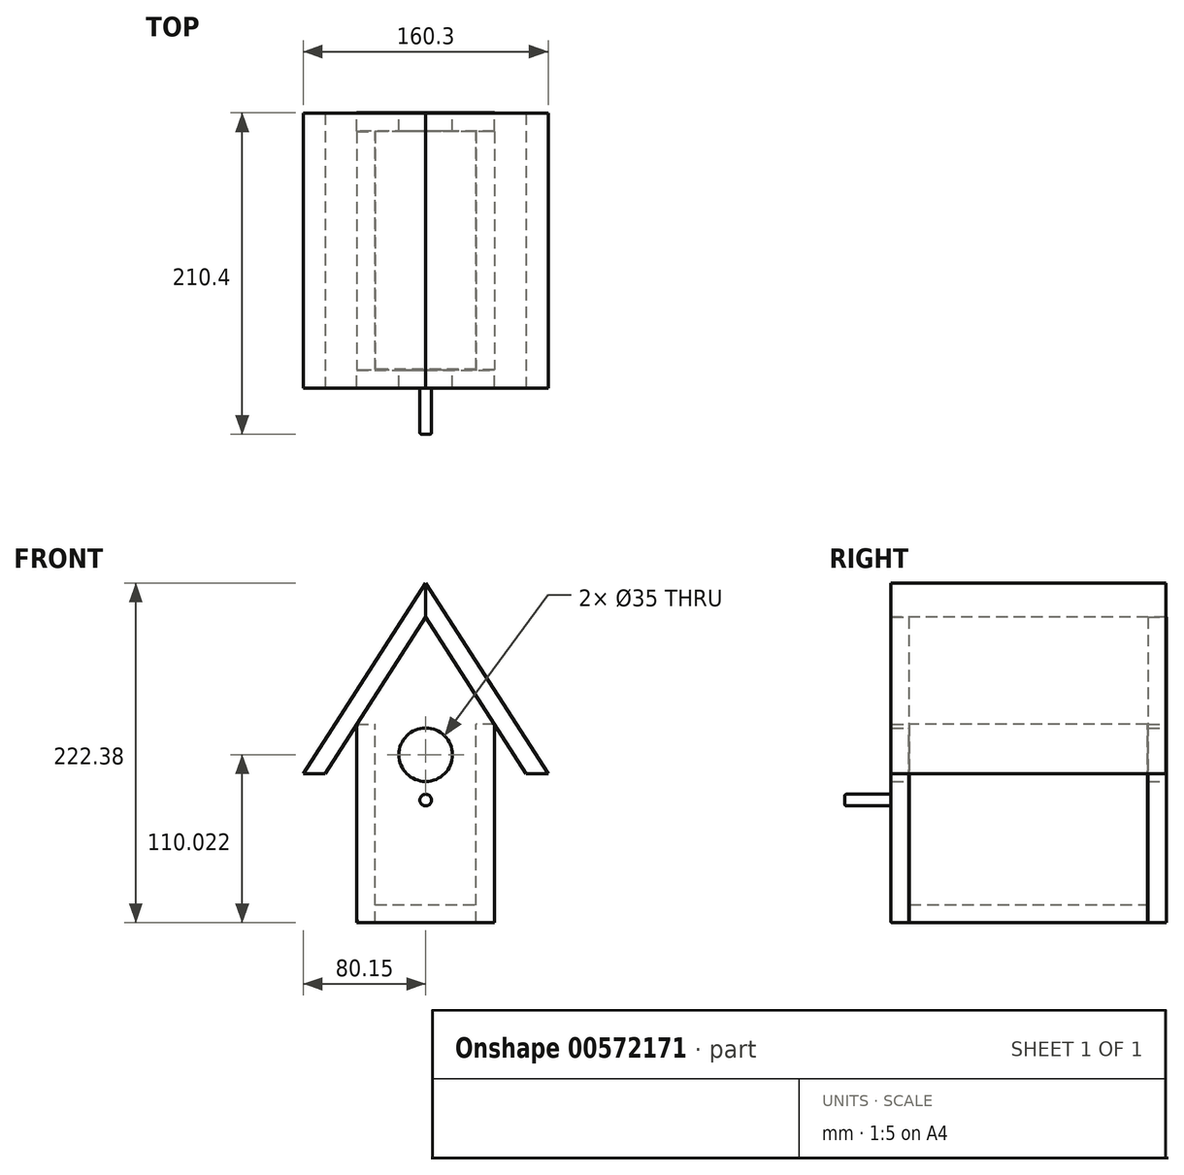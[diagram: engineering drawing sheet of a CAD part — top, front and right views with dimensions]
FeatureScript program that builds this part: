
annotation { "Feature Type Name" : "Feature", "Feature Type Description" : "" }
export const myFeature = defineFeature(function(context is Context, id is Id, definition is map)
    precondition{}
    {
        {
            var Q0;
            Q0=qCreatedBy(makeId("Front.planeOp"),FACE);
            var sketch = newSketch(context, id + "F0", { "sketchPlane" : qUnion([Q0])});
            skLineSegment(sketch, "E0.top", {"start": v(45, -65) * mm, "end": v(-45, -65) * mm});
            skLineSegment(sketch, "E0.left", {"start": v(45, 65) * mm, "end": v(45, -65) * mm});
            skLineSegment(sketch, "E0.right", {"start": v(-45, 65) * mm, "end": v(-45, -65) * mm});
            skPoint(sketch, "E0.middle", {"position": v(0, 0) * mm});
            skLineSegment(sketch, "E1", {"start": v(-45, 65) * mm, "end": v(0, 135) * mm});
            skLineSegment(sketch, "E2", {"start": v(0, 135) * mm, "end": v(45, 65) * mm});
            skLineSegment(sketch, "E3", {"start": v(0, 135) * mm, "end": v(0, -65) * mm, "construction": true});
            skCircle(sketch, "E4", {"center": v(0, 45.02) * mm, "radius": 17.5 * mm});
            skLineSegment(sketch, "E5", {"start": v(0, 135) * mm, "end": v(0, 201.69) * mm, "construction": true});
            skLineSegment(sketch, "E6", {"start": v(0, 45.02) * mm, "end": v(-107.5, 45.02) * mm, "construction": true});
            skLineSegment(sketch, "E7", {"start": v(0, 45.02) * mm, "end": v(114.17, 45.02) * mm, "construction": true});
            skSolve(sketch);
        }
        {
            var Q0;
            Q0=makeQuery(id+"F0.imprint","IMPRINT",FACE,{"disambiguationData":[TD([[makeQuery(id+"F0.imprint","IMPRINT",EDGE,{"derivedFrom":sQuery(id+"F0.wireOp",EDGE,"E0.top")}),-1.0]])]});
            extrude(context, id + "F1", {"entities" : qUnion([Q0]), "depth" : 12 * mm, "offsetDistance" : 25 * mm});
        }
        {
            var Q0;
            Q0=makeQuery(id+"F1.opExtrude","CAP_FACE",FACE,{"disambiguationData":[OSD([sQuery(id+"F0.wireOp",EDGE,"E0.top"),sQuery(id+"F0.wireOp",EDGE,"E0.left"),sQuery(id+"F0.wireOp",EDGE,"E0.right"),sQuery(id+"F0.wireOp",EDGE,"E1"),sQuery(id+"F0.wireOp",EDGE,"E2"),sQuery(id+"F0.wireOp",EDGE,"E4")])],"isStart":false});
            var sketch = newSketch(context, id + "F2", { "sketchPlane" : qUnion([Q0])});
            skLineSegment(sketch, "E8", {"start": v(0, 157.38) * mm, "end": v(80.15, 32.7) * mm});
            skLineSegment(sketch, "E9", {"start": v(80.15, 32.7) * mm, "end": v(65.76, 32.7) * mm});
            skLineSegment(sketch, "E10", {"start": v(65.76, 32.7) * mm, "end": v(0, 135) * mm});
            skLineSegment(sketch, "E11", {"start": v(0, 157.38) * mm, "end": v(0, 135) * mm});
            skLineSegment(sketch, "E12.MirrorCS", {"start": v(-65.76, 32.7) * mm, "end": v(0, 135) * mm});
            skLineSegment(sketch, "E13.MirrorCS", {"start": v(0, 157.38) * mm, "end": v(-80.15, 32.7) * mm});
            skLineSegment(sketch, "E14.MirrorCS", {"start": v(-80.15, 32.7) * mm, "end": v(-65.76, 32.7) * mm});
            skSolve(sketch);
        }
        {
            var Q0;
            Q0=makeQuery(id+"F2.imprint","IMPRINT",FACE,{"disambiguationData":[TD([[makeQuery(id+"F2.imprint","IMPRINT",EDGE,{"derivedFrom":sQuery(id+"F2.wireOp",EDGE,"E11")}),-1.0]])]});
            extrude(context, id + "F3", {"entities" : qUnion([Q0]), "oppositeDirection" : true, "depth" : 180 * mm, "offsetDistance" : 25 * mm});
        }
        {
            var Q0;
            Q0=makeQuery(id+"F2.imprint","IMPRINT",FACE,{"disambiguationData":[TD([[makeQuery(id+"F2.imprint","IMPRINT",EDGE,{"derivedFrom":sQuery(id+"F2.wireOp",EDGE,"E8")}),-1.0]])]});
            extrude(context, id + "F4", {"entities" : qUnion([Q0]), "oppositeDirection" : true, "depth" : 180 * mm, "offsetDistance" : 25 * mm});
        }
        {
            var Q0;
            Q0=makeQuery(id+"F1.opExtrude","CAP_FACE",FACE,{"disambiguationData":[OSD([sQuery(id+"F0.wireOp",EDGE,"E0.top"),sQuery(id+"F0.wireOp",EDGE,"E0.left"),sQuery(id+"F0.wireOp",EDGE,"E0.right"),sQuery(id+"F0.wireOp",EDGE,"E1"),sQuery(id+"F0.wireOp",EDGE,"E2"),sQuery(id+"F0.wireOp",EDGE,"E4")])],"isStart":false});
            var sketch = newSketch(context, id + "F5", { "sketchPlane" : qUnion([Q0])});
            skLineSegment(sketch, "E15.bottom", {"start": v(45, -65) * mm, "end": v(33, -65) * mm});
            skLineSegment(sketch, "E15.top", {"start": v(45, 65) * mm, "end": v(33, 65) * mm});
            skLineSegment(sketch, "E15.left", {"start": v(45, -65) * mm, "end": v(45, 65) * mm});
            skLineSegment(sketch, "E15.right", {"start": v(33, -65) * mm, "end": v(33, 65) * mm});
            skLineSegment(sketch, "E16", {"start": v(0, 0) * mm, "end": v(0, -56.81) * mm, "construction": true});
            skSolve(sketch);
        }
        {
            var Q0;
            Q0 = qSketchRegion(id + "F5", true);
            extrude(context, id + "F6", {"entities" : qUnion([Q0]), "oppositeDirection" : true, "depth" : 168 * mm, "offsetDistance" : 25 * mm, "hasSecondDirection" : true, "secondDirectionOppositeDirection" : true, "secondDirectionDepth" : 12.3 * mm});
        }
        {
            var Q0;
            Q0=makeQuery(id+"F6.opExtrude","SWEPT_BODY",BODY,{"disambiguationData":[OSD([sQuery(id+"F5.wireOp",EDGE,"E15.bottom"),sQuery(id+"F5.wireOp",EDGE,"E15.top"),sQuery(id+"F5.wireOp",EDGE,"E15.left"),sQuery(id+"F5.wireOp",EDGE,"E15.right")])]});
            var Q1;
            Q1=qCreatedBy(makeId("Right.planeOp"),FACE);
            mirror(context, id + "F7", {"operationType" : NewBodyOperationType.ADD, "entities" : qUnion([Q0]), "mirrorPlane" : qUnion([Q1])});
        }
        {
            var Q0;
            Q0=makeQuery(id+"F1.opExtrude","SWEPT_BODY",BODY,{"disambiguationData":[OSD([sQuery(id+"F0.wireOp",EDGE,"E0.top"),sQuery(id+"F0.wireOp",EDGE,"E0.left"),sQuery(id+"F0.wireOp",EDGE,"E0.right"),sQuery(id+"F0.wireOp",EDGE,"E1"),sQuery(id+"F0.wireOp",EDGE,"E2"),sQuery(id+"F0.wireOp",EDGE,"E4")])]});
            transform(context, id + "F8", {"entities" : qUnion([Q0]), "transformType" : TransformType.TRANSLATION_3D, "dx" : 0 * mm, "dy" : 168.4 * mm, "dz" : 0 * mm, "makeCopy" : true});
        }
        {
            var Q0;
            Q0=makeQuery(id+"F8.opPattern","COPY",FACE,{"derivedFrom":makeQuery(id+"F1.opExtrude","CAP_FACE",FACE,{"disambiguationData":[OSD([sQuery(id+"F0.wireOp",EDGE,"E0.top"),sQuery(id+"F0.wireOp",EDGE,"E0.left"),sQuery(id+"F0.wireOp",EDGE,"E0.right"),sQuery(id+"F0.wireOp",EDGE,"E1"),sQuery(id+"F0.wireOp",EDGE,"E2"),sQuery(id+"F0.wireOp",EDGE,"E4")])],"isStart":true}),"instanceName":"1"});
            var sketch = newSketch(context, id + "F9", { "sketchPlane" : qUnion([Q0])});
            skLineSegment(sketch, "E17.bottom", {"start": v(33, -65) * mm, "end": v(-33, -65) * mm});
            skLineSegment(sketch, "E17.top", {"start": v(33, -53) * mm, "end": v(-33, -53) * mm});
            skLineSegment(sketch, "E17.left", {"start": v(33, -65) * mm, "end": v(33, -53) * mm});
            skLineSegment(sketch, "E17.right", {"start": v(-33, -65) * mm, "end": v(-33, -53) * mm});
            skLineSegment(sketch, "E18", {"start": v(33, -59) * mm, "end": v(0, -59) * mm});
            skLineSegment(sketch, "E19", {"start": v(0, -59) * mm, "end": v(-33, -59) * mm});
            skSolve(sketch);
        }
        {
            var Q0;
            Q0 = qSketchRegion(id + "F9", true);
            extrude(context, id + "F10", {"entities" : qUnion([Q0]), "oppositeDirection" : true, "depth" : 168 * mm, "offsetDistance" : 25 * mm, "hasSecondDirection" : true, "secondDirectionOppositeDirection" : true, "secondDirectionDepth" : 12.3 * mm});
        }
        {
            var Q0;
            Q0=makeQuery(id+"F1.opExtrude","CAP_FACE",FACE,{"disambiguationData":[OSD([sQuery(id+"F0.wireOp",EDGE,"E0.top"),sQuery(id+"F0.wireOp",EDGE,"E0.left"),sQuery(id+"F0.wireOp",EDGE,"E0.right"),sQuery(id+"F0.wireOp",EDGE,"E1"),sQuery(id+"F0.wireOp",EDGE,"E2"),sQuery(id+"F0.wireOp",EDGE,"E4")])],"isStart":false});
            var sketch = newSketch(context, id + "F11", { "sketchPlane" : qUnion([Q0])});
            skCircle(sketch, "E20", {"center": v(0, 15.33) * mm, "radius": 3.8 * mm});
            skSolve(sketch);
        }
        {
            var Q0;
            Q0=makeQuery(id+"F11.imprint","IMPRINT",FACE,{"disambiguationData":[TD([[makeQuery(id+"F11.imprint","IMPRINT",EDGE,{"derivedFrom":sQuery(id+"F11.wireOp",EDGE,"E20")}),1.0]])]});
            extrude(context, id + "F12", {"entities" : qUnion([Q0]), "depth" : 30 * mm, "offsetDistance" : 25 * mm});
        }
        {
            var Q0;
            Q0=makeQuery(id+"F12.opExtrude","CAP_EDGE",EDGE,{"disambiguationData":[OSD([sQuery(id+"F11.wireOp",EDGE,"E20")])],"isStart":false});
            fillet(context, id + "F13", {"entities" : qUnion([Q0]), "radius" : 1 * mm, "tangentPropagation" : true, "allowEdgeOverflow" : false});
        }
        {
            var Q0;
            Q0=makeQuery(id+"F1.opExtrude","CAP_FACE",FACE,{"disambiguationData":[OSD([sQuery(id+"F0.wireOp",EDGE,"E0.top"),sQuery(id+"F0.wireOp",EDGE,"E0.left"),sQuery(id+"F0.wireOp",EDGE,"E0.right"),sQuery(id+"F0.wireOp",EDGE,"E1"),sQuery(id+"F0.wireOp",EDGE,"E2"),sQuery(id+"F0.wireOp",EDGE,"E4")])],"isStart":false});
            fillet(context, id + "F14", {"entities" : qUnion([Q0]), "radius" : 1 * mm, "tangentPropagation" : true, "allowEdgeOverflow" : false});
        }
    });
